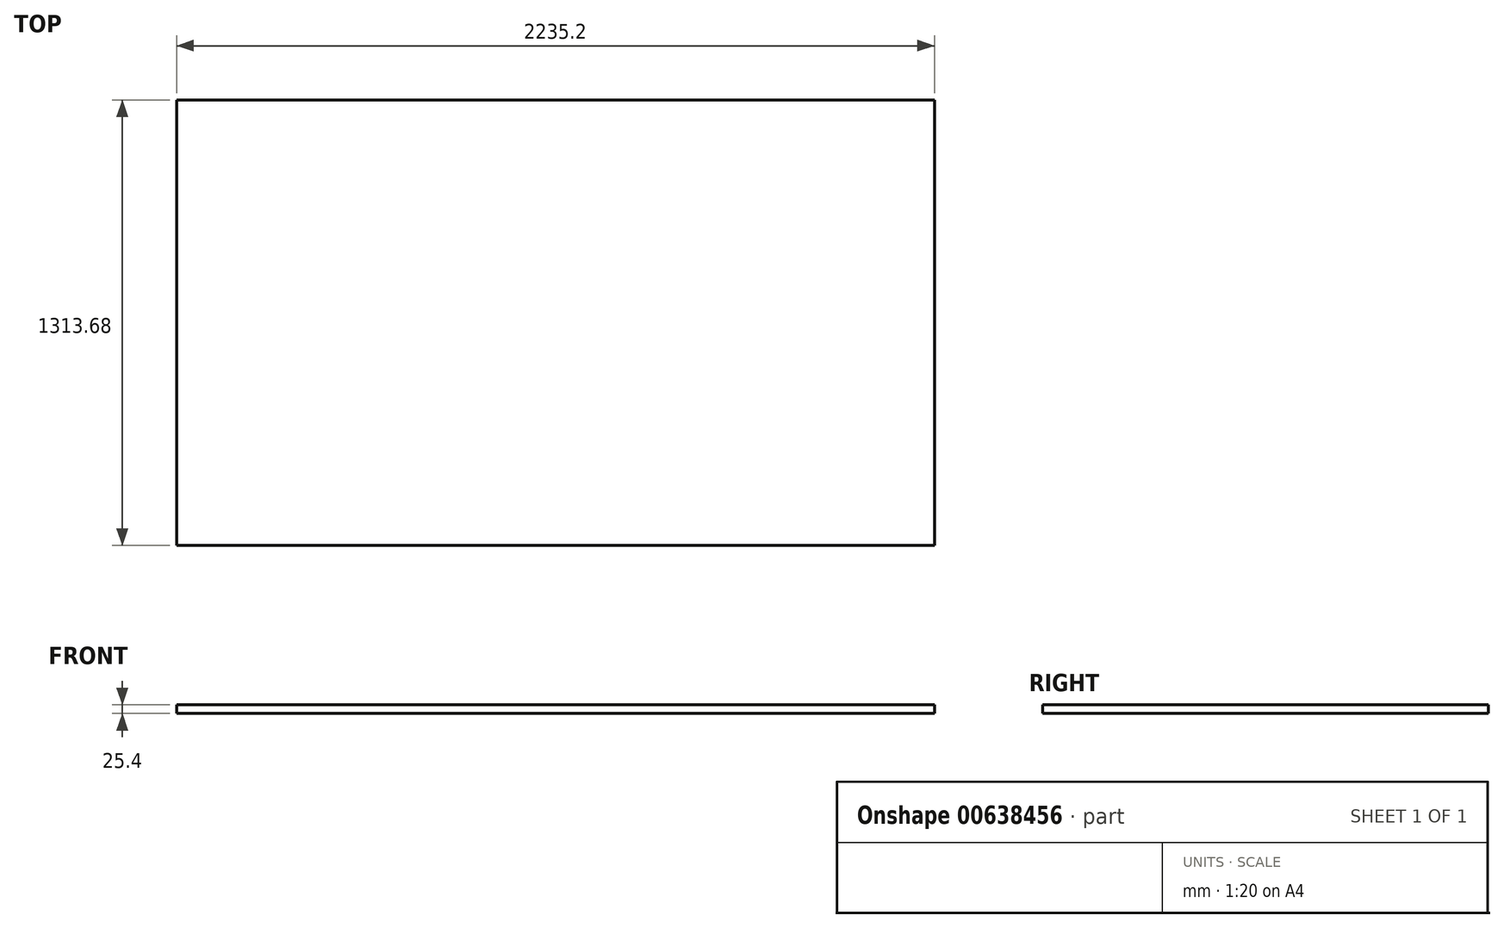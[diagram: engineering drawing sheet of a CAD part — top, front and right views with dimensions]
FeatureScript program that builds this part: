
annotation { "Feature Type Name" : "Feature", "Feature Type Description" : "" }
export const myFeature = defineFeature(function(context is Context, id is Id, definition is map)
    precondition{}
    {
        {
            var Q0;
            Q0=qCreatedBy(makeId("Top.planeOp"),FACE);
            var sketch = newSketch(context, id + "F0", { "sketchPlane" : qUnion([Q0])});
            skLineSegment(sketch, "E0.bottom", {"start": v(1117.6, 656.84) * mm, "end": v(-1117.6, 656.84) * mm});
            skLineSegment(sketch, "E0.top", {"start": v(1117.6, -656.84) * mm, "end": v(-1117.6, -656.84) * mm});
            skLineSegment(sketch, "E0.left", {"start": v(1117.6, 656.84) * mm, "end": v(1117.6, -656.84) * mm});
            skLineSegment(sketch, "E0.right", {"start": v(-1117.6, 656.84) * mm, "end": v(-1117.6, -656.84) * mm});
            skPoint(sketch, "E0.middle", {"position": v(0, 0) * mm});
            skSolve(sketch);
        }
        {
            var Q0;
            Q0=makeQuery(id+"F0.imprint","IMPRINT",FACE,{"disambiguationData":[TD([[makeQuery(id+"F0.imprint","IMPRINT",EDGE,{"derivedFrom":sQuery(id+"F0.wireOp",EDGE,"E0.bottom")}),1.0]])]});
            extrude(context, id + "F1", {"entities" : qUnion([Q0]), "depth" : 25.4 * mm, "offsetDistance" : 25.4 * mm});
        }
    });
